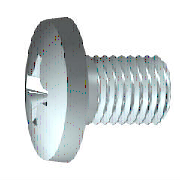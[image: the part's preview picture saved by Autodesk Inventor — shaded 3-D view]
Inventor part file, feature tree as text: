
AUTODESK INVENTOR PART (.ipt)
format: ipt  version: 2014 SP1 (Build 180222100, 222)  size: 266,240 bytes
history: native  units: mm (DEFAULTED — no unit token found)
features: other x2, extrude x1, plane x1
ambient origin geometry x7: Origin, YZ Plane, XZ Plane, X Axis, Y Axis, Z Axis, Center Point
bodies: Solid1 (feature_tree), Body (feature_tree)
feature tree (4):
  other  "IDS_WORKPLANE{1}"
  extrude  "Slot"  Depth=4.826mm
  other  "Cut"
  plane  "Work Plane3"
